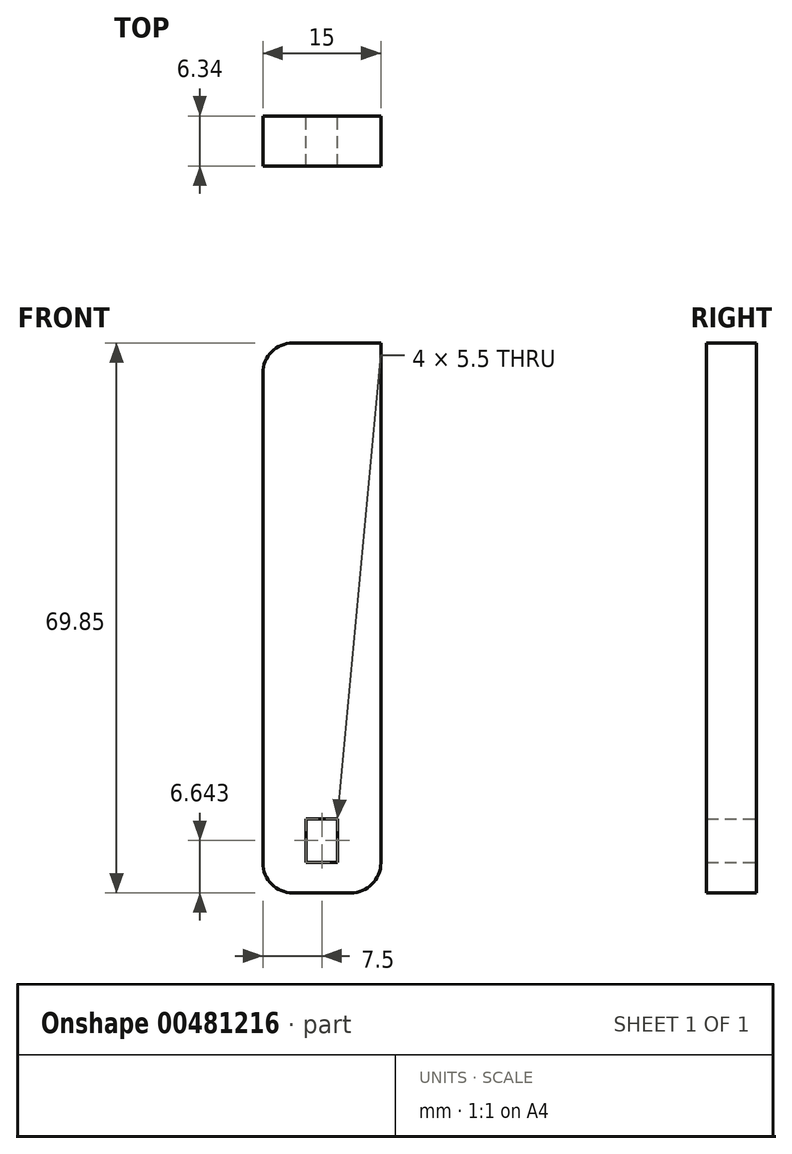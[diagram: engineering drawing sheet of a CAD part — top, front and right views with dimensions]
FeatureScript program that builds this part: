
annotation { "Feature Type Name" : "Feature", "Feature Type Description" : "" }
export const myFeature = defineFeature(function(context is Context, id is Id, definition is map)
    precondition{}
    {
        {
            var Q0;
            Q0=qCreatedBy(makeId("Front.planeOp"),FACE);
            var sketch = newSketch(context, id + "F0", { "sketchPlane" : qUnion([Q0])});
            skLineSegment(sketch, "E0.bottom", {"start": v(-3.69, 0) * mm, "end": v(3.7, 0) * mm});
            skLineSegment(sketch, "E0.top", {"start": v(-3.7, -69.85) * mm, "end": v(3.69, -69.85) * mm});
            skLineSegment(sketch, "E0.left", {"start": v(-7.5, -3.81) * mm, "end": v(-7.5, -66.04) * mm});
            skLineSegment(sketch, "E0.right", {"start": v(7.5, 0) * mm, "end": v(7.5, -66.04) * mm});
            skPoint(sketch, "E0.middle", {"position": v(0, -34.92) * mm});
            skLineSegment(sketch, "E1.bottom", {"start": v(7.5, 0) * mm, "end": v(-3.89, 0) * mm});
            skPoint(sketch, "E1.middle", {"position": v(0, 33.8) * mm});
            skLineSegment(sketch, "E2.bottom", {"start": v(-2, -60.46) * mm, "end": v(2, -60.46) * mm});
            skLineSegment(sketch, "E2.top", {"start": v(-2, -65.96) * mm, "end": v(2, -65.96) * mm});
            skLineSegment(sketch, "E2.left", {"start": v(-2, -60.46) * mm, "end": v(-2, -65.96) * mm});
            skLineSegment(sketch, "E2.right", {"start": v(2, -60.46) * mm, "end": v(2, -65.96) * mm});
            skPoint(sketch, "E2.middle", {"position": v(0, -63.2) * mm});
            skPoint(sketch, "E3.visualSharp", {"position": v(7.5, -69.85) * mm});
            skArc(sketch, "E3.filletArc", {"start": v(3.69, -69.85) * mm, "mid": v(6.38, -68.73) * mm, "end": v(7.5, -66.04) * mm});
            skPoint(sketch, "E4.visualSharp", {"position": v(-7.5, -69.85) * mm});
            skArc(sketch, "E4.filletArc", {"start": v(-7.5, -66.04) * mm, "mid": v(-6.38, -68.73) * mm, "end": v(-3.7, -69.85) * mm});
            skPoint(sketch, "E5.visualSharp", {"position": v(7.5, 0) * mm});
            skPoint(sketch, "E6.visualSharp", {"position": v(-7.5, 0) * mm});
            skArc(sketch, "E6.filletArc", {"start": v(-3.69, 0) * mm, "mid": v(-6.38, -1.12) * mm, "end": v(-7.5, -3.81) * mm});
            skSolve(sketch);
        }
        {
            var Q0;
            Q0=makeQuery(id+"F0.imprint","IMPRINT",FACE,{"disambiguationData":[TD([[makeQuery(id+"F0.imprint","IMPRINT",EDGE,{"derivedFrom":sQuery(id+"F0.wireOp",EDGE,"E0.top")}),1.0]])]});
            extrude(context, id + "F1", {"entities" : qUnion([Q0]), "endBound" : BoundingType.SYMMETRIC, "depth" : 6.35 * mm});
        }
    });
